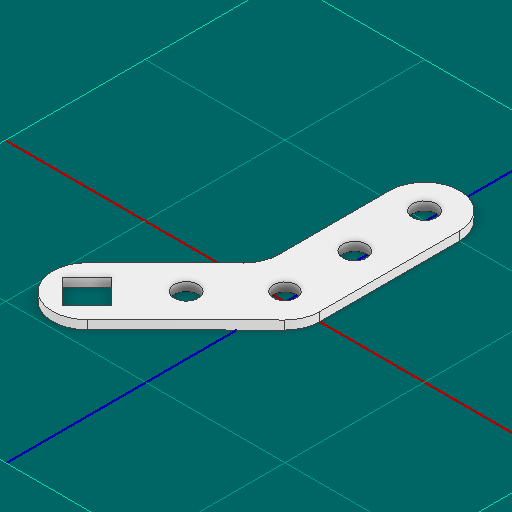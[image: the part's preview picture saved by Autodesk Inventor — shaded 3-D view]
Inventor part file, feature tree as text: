
AUTODESK INVENTOR PART (.ipt)
format: ipt  version: 2025 (Build 290162000, 162)  size: 131,584 bytes
history: native  units: in
note: dims shown in document units (in); Inventor stores cm internally (conversion verified against a paired STEP export)
features: other x3, extrude x1, sketch x1
ambient origin geometry x8: Origin, YZ Plane, XZ Plane, XY Plane, X Axis, Y Axis, Z Axis, Center Point
bodies: Solid1 (feature_tree)
feature tree (5):
  other  "Blocks"
  extrude  "Extrusion1"  Depth=0.5in
  sketch  "Sketch1"  dims[d0=0.5in d5=0.5in d6=0.25in d7=0.0625in d8=0.0in d9=0.248in d10=45.0deg d11=0.248in]
  other  "main"
  other  "main:1"
